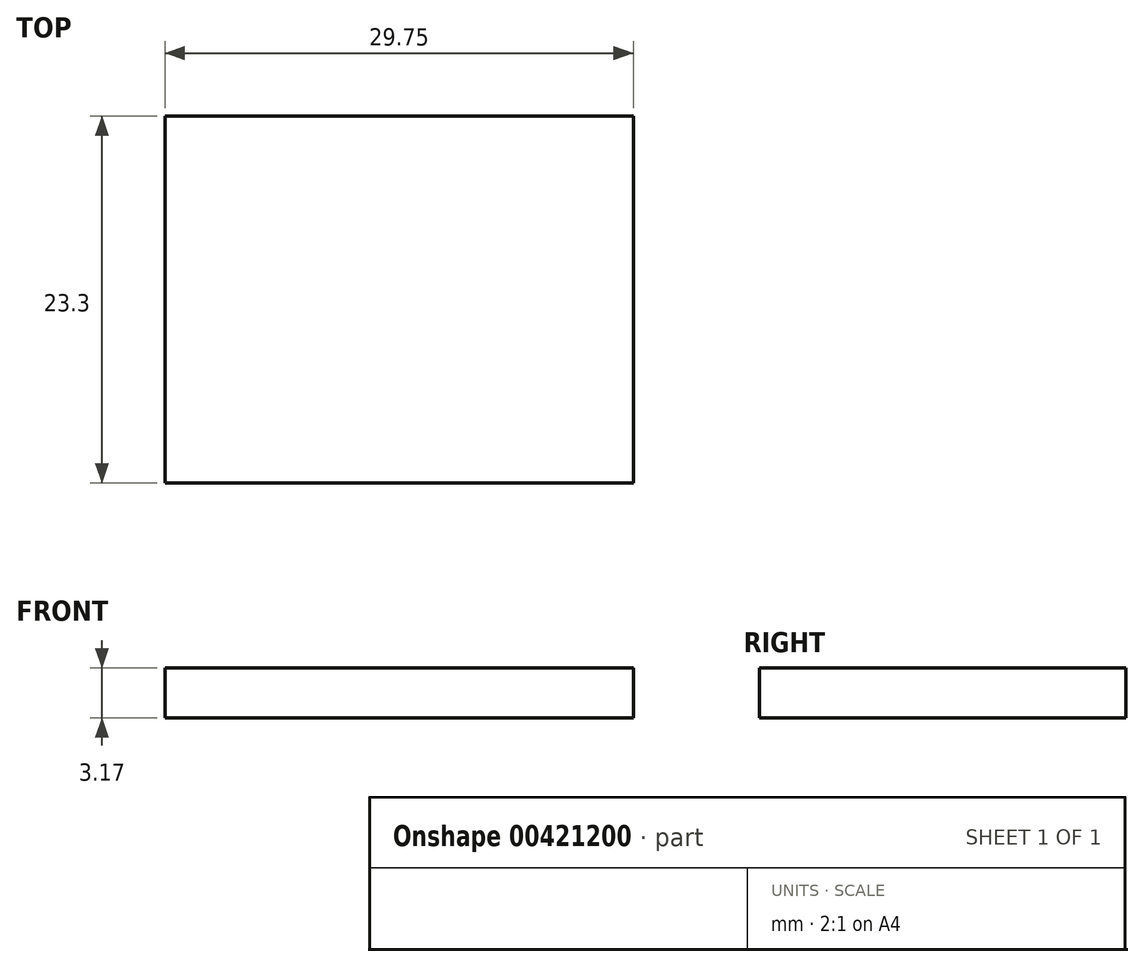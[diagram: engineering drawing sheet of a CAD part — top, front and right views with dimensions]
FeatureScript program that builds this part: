
annotation { "Feature Type Name" : "Feature", "Feature Type Description" : "" }
export const myFeature = defineFeature(function(context is Context, id is Id, definition is map)
    precondition{}
    {
        {
            var Q0;
            Q0=qCreatedBy(makeId("Top.planeOp"),FACE);
            var sketch = newSketch(context, id + "F0", { "sketchPlane" : qUnion([Q0])});
            skLineSegment(sketch, "E0.bottom", {"start": v(0, 0) * mm, "end": v(29.75, 0) * mm});
            skLineSegment(sketch, "E0.top", {"start": v(0, 23.3) * mm, "end": v(29.75, 23.3) * mm});
            skLineSegment(sketch, "E0.left", {"start": v(0, 0) * mm, "end": v(0, 23.3) * mm});
            skLineSegment(sketch, "E0.right", {"start": v(29.75, 0) * mm, "end": v(29.75, 23.3) * mm});
            skSolve(sketch);
        }
        {
            var Q0;
            Q0 = qSketchRegion(id + "F0", true);
            extrude(context, id + "F1", {"entities" : qUnion([Q0]), "depth" : 3.17 * mm});
        }
    });
